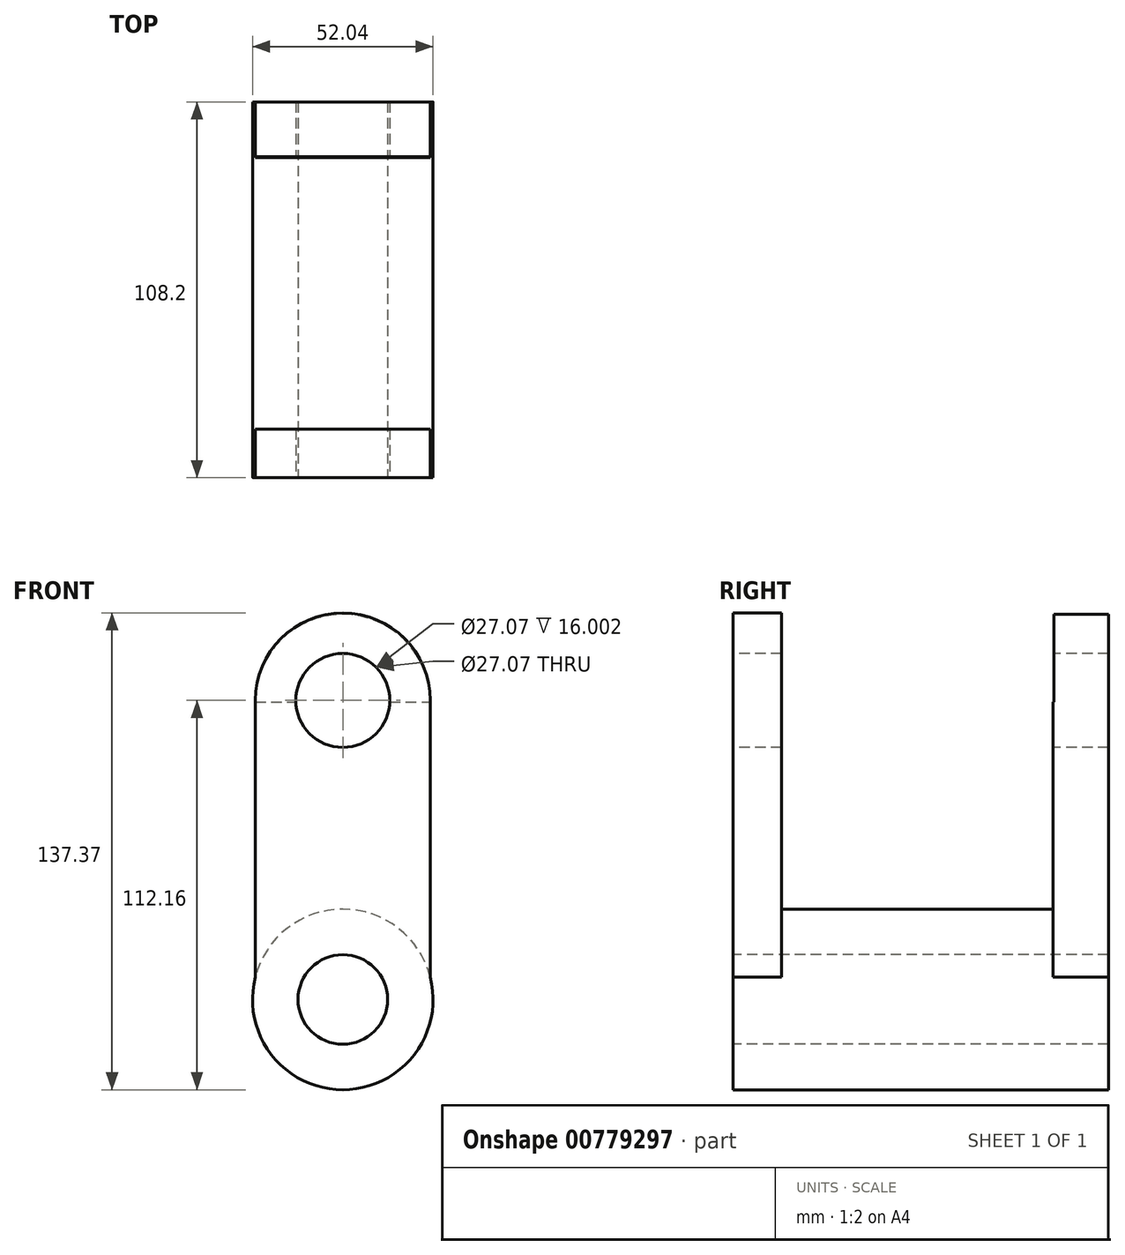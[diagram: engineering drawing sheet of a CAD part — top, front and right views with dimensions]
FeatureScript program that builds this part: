
annotation { "Feature Type Name" : "Feature", "Feature Type Description" : "" }
export const myFeature = defineFeature(function(context is Context, id is Id, definition is map)
    precondition{}
    {
        {
            var Q0;
            Q0=qCreatedBy(makeId("Front.planeOp"),FACE);
            var sketch = newSketch(context, id + "F0", { "sketchPlane" : qUnion([Q0])});
            skCircle(sketch, "E0", {"center": v(-32.46, 6.44) * mm, "radius": 26.02 * mm});
            skSolve(sketch);
        }
        {
            var Q0;
            Q0 = qSketchRegion(id + "F0", true);
            extrude(context, id + "F1", {"entities" : qUnion([Q0]), "depth" : 108.2 * mm, "offsetDistance" : 25.4 * mm});
        }
        {
            var Q0;
            Q0=makeQuery(id+"F1.opExtrude","CAP_FACE",FACE,{"disambiguationData":[OSD([sQuery(id+"F0.wireOp",EDGE,"E0")])],"isStart":false});
            var sketch = newSketch(context, id + "F2", { "sketchPlane" : qUnion([Q0])});
            skLineSegment(sketch, "E1.bottom", {"start": v(-7.25, 0) * mm, "end": v(-57.67, 0) * mm});
            skLineSegment(sketch, "E1.top", {"start": v(-7.25, 92.58) * mm, "end": v(-57.67, 92.58) * mm});
            skLineSegment(sketch, "E1.left", {"start": v(-7.25, 0) * mm, "end": v(-7.25, 92.58) * mm});
            skLineSegment(sketch, "E1.right", {"start": v(-57.67, 0) * mm, "end": v(-57.67, 92.58) * mm});
            skSolve(sketch);
        }
        {
            var Q0;
            Q0 = qSketchRegion(id + "F2", true);
            extrude(context, id + "F3", {"entities" : qUnion([Q0]), "operationType" : NewBodyOperationType.ADD, "oppositeDirection" : true, "depth" : 13.97 * mm, "offsetDistance" : 25.4 * mm});
        }
        {
            var Q0;
            Q0=makeQuery(id+"F1.opExtrude","CAP_FACE",FACE,{"disambiguationData":[OSD([sQuery(id+"F0.wireOp",EDGE,"E0")])],"isStart":true});
            var sketch = newSketch(context, id + "F4", { "sketchPlane" : qUnion([Q0])});
            skLineSegment(sketch, "E2.bottom", {"start": v(57.67, 0) * mm, "end": v(7.25, 0) * mm});
            skLineSegment(sketch, "E2.top", {"start": v(57.67, 99.27) * mm, "end": v(7.25, 99.27) * mm});
            skLineSegment(sketch, "E2.left", {"start": v(57.67, 0) * mm, "end": v(57.67, 99.27) * mm});
            skLineSegment(sketch, "E2.right", {"start": v(7.25, 0) * mm, "end": v(7.25, 99.27) * mm});
            skSolve(sketch);
        }
        {
            var Q0;
            Q0 = qSketchRegion(id + "F4", true);
            extrude(context, id + "F5", {"entities" : qUnion([Q0]), "operationType" : NewBodyOperationType.ADD, "oppositeDirection" : true, "depth" : 16 * mm, "offsetDistance" : 25.4 * mm});
        }
        {
            var Q0;
            Q0=makeQuery(id+"F5.opExtrude","SWEPT_FACE",FACE,{"disambiguationData":[OSD([sQuery(id+"F4.wireOp",EDGE,"E2.right")])]});
            var sketch = newSketch(context, id + "F6", { "sketchPlane" : qUnion([Q0])});
            skLineSegment(sketch, "E3.bottom", {"start": v(0, 99.27) * mm, "end": v(-16, 99.27) * mm});
            skLineSegment(sketch, "E3.top", {"start": v(0, 92.18) * mm, "end": v(-16, 92.18) * mm});
            skLineSegment(sketch, "E3.left", {"start": v(0, 99.27) * mm, "end": v(0, 92.18) * mm});
            skLineSegment(sketch, "E3.right", {"start": v(-16, 99.27) * mm, "end": v(-16, 92.18) * mm});
            skSolve(sketch);
        }
        {
            var Q0;
            Q0 = qSketchRegion(id + "F6", true);
            extrude(context, id + "F7", {"entities" : qUnion([Q0]), "operationType" : NewBodyOperationType.REMOVE, "oppositeDirection" : true, "depth" : 64 * mm, "offsetDistance" : 25.4 * mm});
        }
        {
            var Q0;
            Q0=makeQuery(id+"F3.boolean.opBoolean","MERGE",FACE,{"derivedFrom":[makeQuery(id+"F1.opExtrude","CAP_FACE",FACE,{"disambiguationData":[OSD([sQuery(id+"F0.wireOp",EDGE,"E0")])],"isStart":false}),makeQuery(id+"F3.opExtrude","CAP_FACE",FACE,{"disambiguationData":[OSD([sQuery(id+"F2.wireOp",EDGE,"E1.bottom"),sQuery(id+"F2.wireOp",EDGE,"E1.top"),sQuery(id+"F2.wireOp",EDGE,"E1.left"),sQuery(id+"F2.wireOp",EDGE,"E1.right")])],"isStart":true})]});
            var sketch = newSketch(context, id + "F8", { "sketchPlane" : qUnion([Q0])});
            skCircle(sketch, "E4", {"center": v(-32.46, 6.44) * mm, "radius": 12.9 * mm});
            skSolve(sketch);
        }
        {
            var Q0;
            Q0 = qSketchRegion(id + "F8", true);
            extrude(context, id + "F9", {"entities" : qUnion([Q0]), "operationType" : NewBodyOperationType.REMOVE, "oppositeDirection" : true, "depth" : 152.15 * mm, "offsetDistance" : 25.4 * mm});
        }
        {
            var Q0;
            Q0=makeQuery(id+"F5.boolean.opBoolean","MERGE",FACE,{"derivedFrom":[makeQuery(id+"F1.opExtrude","CAP_FACE",FACE,{"disambiguationData":[OSD([sQuery(id+"F0.wireOp",EDGE,"E0")])],"isStart":true}),makeQuery(id+"F5.opExtrude","CAP_FACE",FACE,{"disambiguationData":[OSD([sQuery(id+"F4.wireOp",EDGE,"E2.bottom"),sQuery(id+"F4.wireOp",EDGE,"E2.top"),sQuery(id+"F4.wireOp",EDGE,"E2.left"),sQuery(id+"F4.wireOp",EDGE,"E2.right")])],"isStart":true})]});
            var sketch = newSketch(context, id + "F10", { "sketchPlane" : qUnion([Q0])});
            skArc(sketch, "E5", {"start": v(57.67, 92.18) * mm, "mid": v(32.46, 117.39) * mm, "end": v(7.25, 92.18) * mm});
            skSolve(sketch);
        }
        {
            var Q0;
            Q0=makeQuery(id+"F10.imprint","IMPRINT",FACE,{"disambiguationData":[TD([[makeQuery(id+"F10.imprint","IMPRINT",EDGE,{"derivedFrom":sQuery(id+"F10.wireOp",EDGE,"E5")}),1.0]])]});
            extrude(context, id + "F11", {"entities" : qUnion([Q0]), "operationType" : NewBodyOperationType.ADD, "oppositeDirection" : true, "depth" : 15.75 * mm, "offsetDistance" : 25.4 * mm});
        }
        {
            var Q0;
            Q0=makeQuery(id+"F3.boolean.opBoolean","MERGE",FACE,{"derivedFrom":[makeQuery(id+"F1.opExtrude","CAP_FACE",FACE,{"disambiguationData":[OSD([sQuery(id+"F0.wireOp",EDGE,"E0")])],"isStart":false}),makeQuery(id+"F3.opExtrude","CAP_FACE",FACE,{"disambiguationData":[OSD([sQuery(id+"F2.wireOp",EDGE,"E1.bottom"),sQuery(id+"F2.wireOp",EDGE,"E1.top"),sQuery(id+"F2.wireOp",EDGE,"E1.left"),sQuery(id+"F2.wireOp",EDGE,"E1.right")])],"isStart":true})]});
            var sketch = newSketch(context, id + "F12", { "sketchPlane" : qUnion([Q0])});
            skArc(sketch, "E6", {"start": v(-7.25, 92.58) * mm, "mid": v(-32.46, 117.79) * mm, "end": v(-57.67, 92.58) * mm});
            skSolve(sketch);
        }
        {
            var Q0;
            Q0=makeQuery(id+"F12.imprint","IMPRINT",FACE,{"disambiguationData":[TD([[makeQuery(id+"F12.imprint","IMPRINT",EDGE,{"derivedFrom":sQuery(id+"F12.wireOp",EDGE,"E6")}),1.0]])]});
            extrude(context, id + "F13", {"entities" : qUnion([Q0]), "operationType" : NewBodyOperationType.ADD, "oppositeDirection" : true, "depth" : 13.97 * mm, "offsetDistance" : 25.4 * mm});
        }
        {
            var Q0;
            {var subQ0=sQuery(id+"F2.wireOp",EDGE,"E1.top");Q0=makeQuery(id+"F13.boolean.opBoolean","MERGE",FACE,{"derivedFrom":[makeQuery(id+"F3.boolean.opBoolean","MERGE",FACE,{"derivedFrom":[makeQuery(id+"F1.opExtrude","CAP_FACE",FACE,{"disambiguationData":[OSD([sQuery(id+"F0.wireOp",EDGE,"E0")])],"isStart":false}),makeQuery(id+"F3.opExtrude","CAP_FACE",FACE,{"disambiguationData":[OSD([sQuery(id+"F2.wireOp",EDGE,"E1.bottom"),subQ0,sQuery(id+"F2.wireOp",EDGE,"E1.left"),sQuery(id+"F2.wireOp",EDGE,"E1.right")])],"isStart":true})]}),makeQuery(id+"F13.opExtrude","CAP_FACE",FACE,{"disambiguationData":[OSD([subQ0,sQuery(id+"F12.wireOp",EDGE,"E6")])],"isStart":true})]});}
            var sketch = newSketch(context, id + "F14", { "sketchPlane" : qUnion([Q0])});
            skCircle(sketch, "E7", {"center": v(-32.46, 92.58) * mm, "radius": 13.53 * mm});
            skSolve(sketch);
        }
        {
            var Q0;
            Q0 = qSketchRegion(id + "F14", true);
            extrude(context, id + "F15", {"entities" : qUnion([Q0]), "operationType" : NewBodyOperationType.REMOVE, "oppositeDirection" : true, "depth" : 238.25 * mm, "offsetDistance" : 25.4 * mm});
        }
    });
